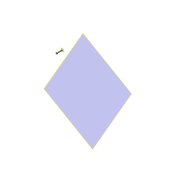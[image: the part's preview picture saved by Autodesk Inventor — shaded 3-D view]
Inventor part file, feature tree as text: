
AUTODESK INVENTOR PART (.ipt)
format: ipt  version: 2016 (Build 200138000, 138)  size: 129,024 bytes
history: native  units: mm
features: sketch x6, extrude x5, plane x2, thread x1, hole x1
ambient origin geometry x8: Origin, YZ Plane, XZ Plane, XY Plane, X Axis, Y Axis, Z Axis, Center Point
bodies: Solid1 (feature_tree)
feature tree (15):
  plane  "Work Plane1"
  extrude  "Extrusion1"  Depth=36.5mm TaperAngle=0.0deg
  extrude  "Extrusion2"  Depth=4.5mm TaperAngle=0.0deg
  thread  "Thread1"  [1 undecoded]
  plane  "Work Plane2"
  extrude  "Extrusion4"  Depth=1.0mm
  hole  "Hole1"  [1 undecoded]
  extrude  "Extrusion5"  Depth=1.0mm
  extrude  "Extrusion6"  Depth=1.0mm TaperAngle=0.0deg
  sketch  "Sketch1"  dims[d0=8.0mm d1=36.5mm d2=0.0mm]
  sketch  "Sketch2"  dims[d3=13.0mm d4=4.5mm d5=0.0mm d11=21.0mm d12=0.0mm]
  sketch  "Sketch4"  dims[d16=1.0mm d17=1.0mm]
  sketch  "Sketch5"  dims[d18=0.9mm d19=0.0mm]
  sketch  "Sketch6"  dims[d20=2.459mm d21=10.0mm d22=5.0mm d23=2.0mm d24=90.0deg d25=13.0mm d26=20.594885mm d27=0.2mm d28=0.0mm]
  sketch  "Sketch7"  dims[d29=5.5mm d30=6.8mm d31=1.0mm d32=0.0mm]
note: 2 required parameter values undecoded (feature->parameter linkage not recoverable at this tier; creation-order binding heuristic only, values carry confidence <= 0.55)
